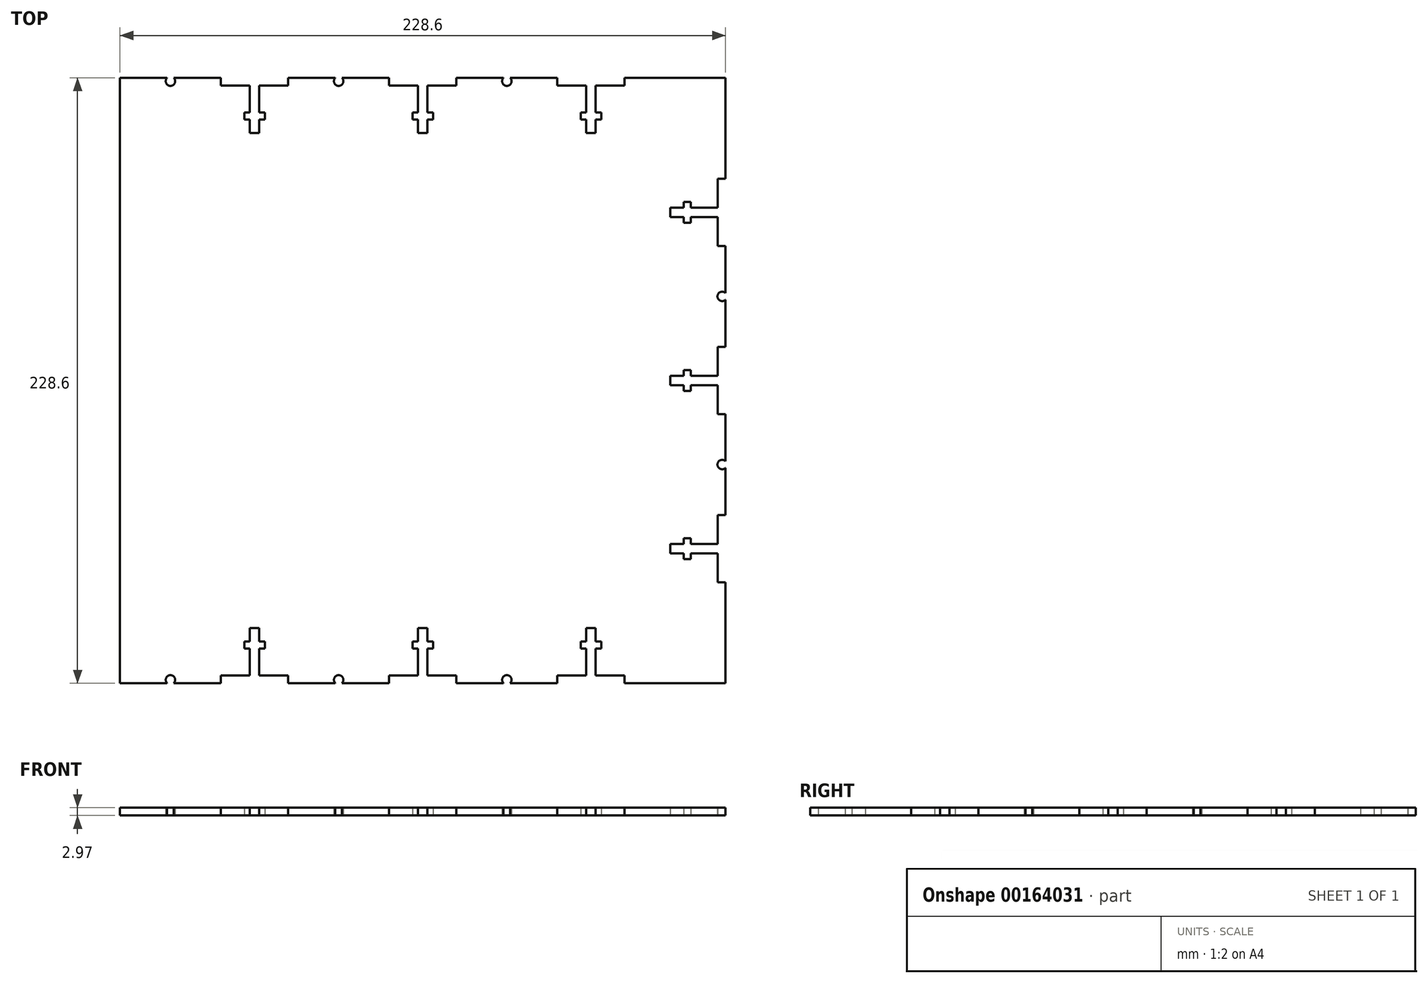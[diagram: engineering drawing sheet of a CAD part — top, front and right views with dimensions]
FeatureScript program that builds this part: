
annotation { "Feature Type Name" : "Feature", "Feature Type Description" : "" }
export const myFeature = defineFeature(function(context is Context, id is Id, definition is map)
    precondition{}
    {
        {
            var Q0;
            Q0=qCreatedBy(makeId("Top.planeOp"),FACE);
            var sketch = newSketch(context, id + "F0", { "sketchPlane" : qUnion([Q0])});
            skLineSegment(sketch, "E0.bottom", {"start": v(114.3, -114.3) * mm, "end": v(-114.3, -114.3) * mm});
            skLineSegment(sketch, "E0.top", {"start": v(114.3, 114.3) * mm, "end": v(-114.3, 114.3) * mm});
            skLineSegment(sketch, "E0.left", {"start": v(114.3, -114.3) * mm, "end": v(114.3, 114.3) * mm});
            skLineSegment(sketch, "E0.right", {"start": v(-114.3, -114.3) * mm, "end": v(-114.3, 114.3) * mm});
            skPoint(sketch, "E0.middle", {"position": v(0, 0) * mm});
            skLineSegment(sketch, "E1.bottom", {"start": v(-76.2, -114.3) * mm, "end": v(-50.8, -114.3) * mm});
            skLineSegment(sketch, "E1.top", {"start": v(-76.2, -111.33) * mm, "end": v(-65.27, -111.33) * mm});
            skLineSegment(sketch, "E1.left", {"start": v(-76.2, -114.3) * mm, "end": v(-76.2, -111.33) * mm});
            skLineSegment(sketch, "E1.right", {"start": v(-50.8, -114.3) * mm, "end": v(-50.8, -111.33) * mm});
            skArc(sketch, "E2", {"start": v(-94, -114.3) * mm, "mid": v(-95.25, -111.25) * mm, "end": v(-96.5, -114.3) * mm});
            skLineSegment(sketch, "E3.bottom", {"start": v(114.3, 76.2) * mm, "end": v(111.33, 76.2) * mm});
            skLineSegment(sketch, "E3.top", {"start": v(114.3, 50.8) * mm, "end": v(111.33, 50.8) * mm});
            skLineSegment(sketch, "E3.left", {"start": v(114.3, 76.2) * mm, "end": v(114.3, 50.8) * mm});
            skLineSegment(sketch, "E3.right", {"start": v(111.33, 76.2) * mm, "end": v(111.33, 50.8) * mm});
            skLineSegment(sketch, "E4.bottom", {"start": v(114.3, 12.7) * mm, "end": v(111.33, 12.7) * mm});
            skLineSegment(sketch, "E4.top", {"start": v(114.3, -12.7) * mm, "end": v(111.33, -12.7) * mm});
            skLineSegment(sketch, "E4.left", {"start": v(114.3, 12.7) * mm, "end": v(114.3, -12.7) * mm});
            skLineSegment(sketch, "E4.right", {"start": v(111.33, 12.7) * mm, "end": v(111.33, -12.7) * mm});
            skLineSegment(sketch, "E5.bottom", {"start": v(114.3, -50.8) * mm, "end": v(111.33, -50.8) * mm});
            skLineSegment(sketch, "E5.top", {"start": v(114.3, -76.2) * mm, "end": v(111.33, -76.2) * mm});
            skLineSegment(sketch, "E5.left", {"start": v(114.3, -50.8) * mm, "end": v(114.3, -76.2) * mm});
            skLineSegment(sketch, "E5.right", {"start": v(111.33, -50.8) * mm, "end": v(111.33, -61.73) * mm});
            skArc(sketch, "E6", {"start": v(114.3, 33) * mm, "mid": v(111.25, 31.75) * mm, "end": v(114.3, 30.5) * mm});
            skArc(sketch, "E7", {"start": v(114.3, -30.5) * mm, "mid": v(111.25, -31.75) * mm, "end": v(114.3, -33) * mm});
            skLineSegment(sketch, "E8.bottom", {"start": v(-65.27, -114.3) * mm, "end": v(-61.73, -114.3) * mm});
            skLineSegment(sketch, "E8.top", {"start": v(-65.27, -93.5) * mm, "end": v(-61.73, -93.5) * mm});
            skLineSegment(sketch, "E8.left", {"start": v(-65.27, -111.33) * mm, "end": v(-65.27, -101.17) * mm});
            skLineSegment(sketch, "E8.right", {"start": v(-61.73, -111.33) * mm, "end": v(-61.73, -101.17) * mm});
            skPoint(sketch, "E9", {"position": v(-63.5, -114.3) * mm});
            skLineSegment(sketch, "E10.trimOffspring", {"start": v(-61.73, -111.33) * mm, "end": v(-50.8, -111.33) * mm});
            skLineSegment(sketch, "E11", {"start": v(-63.5, -114.3) * mm, "end": v(-63.5, -89.69) * mm, "construction": true});
            skLineSegment(sketch, "E12.bottom", {"start": v(-59.61, -101.17) * mm, "end": v(-61.73, -101.17) * mm});
            skLineSegment(sketch, "E12.top", {"start": v(-59.61, -98.53) * mm, "end": v(-61.73, -98.53) * mm});
            skLineSegment(sketch, "E12.left", {"start": v(-59.61, -101.17) * mm, "end": v(-59.61, -98.53) * mm});
            skLineSegment(sketch, "E12.right", {"start": v(-67.39, -101.17) * mm, "end": v(-67.39, -98.53) * mm});
            skPoint(sketch, "E12.middle", {"position": v(-63.5, -99.85) * mm});
            skLineSegment(sketch, "E13.trimOffspring", {"start": v(-65.27, -98.53) * mm, "end": v(-65.27, -93.5) * mm});
            skLineSegment(sketch, "E14.trimOffspring", {"start": v(-61.73, -98.53) * mm, "end": v(-61.73, -93.5) * mm});
            skLineSegment(sketch, "E15.trimOffspring", {"start": v(-65.27, -98.53) * mm, "end": v(-67.39, -98.53) * mm});
            skLineSegment(sketch, "E16.trimOffspring", {"start": v(-65.27, -101.17) * mm, "end": v(-67.39, -101.17) * mm});
            skArc(sketch, "E17.1.0.0", {"start": v(-30.5, -114.3) * mm, "mid": v(-31.75, -111.25) * mm, "end": v(-33, -114.3) * mm});
            skLineSegment(sketch, "E17.1.0.1", {"start": v(-12.7, -114.3) * mm, "end": v(-12.7, -111.33) * mm});
            skLineSegment(sketch, "E17.1.0.2", {"start": v(-12.7, -114.3) * mm, "end": v(12.7, -114.3) * mm});
            skLineSegment(sketch, "E17.1.0.3", {"start": v(1.77, -111.33) * mm, "end": v(12.7, -111.33) * mm});
            skLineSegment(sketch, "E17.1.0.4", {"start": v(12.7, -114.3) * mm, "end": v(12.7, -111.33) * mm});
            skLineSegment(sketch, "E17.1.0.5", {"start": v(-12.7, -111.33) * mm, "end": v(-1.77, -111.33) * mm});
            skLineSegment(sketch, "E17.1.0.6", {"start": v(-1.77, -111.33) * mm, "end": v(-1.77, -101.17) * mm});
            skLineSegment(sketch, "E17.1.0.7", {"start": v(1.77, -111.33) * mm, "end": v(1.77, -101.17) * mm});
            skLineSegment(sketch, "E17.1.0.8", {"start": v(1.77, -98.53) * mm, "end": v(1.77, -93.5) * mm});
            skLineSegment(sketch, "E17.1.0.9", {"start": v(-1.77, -98.53) * mm, "end": v(-1.77, -93.5) * mm});
            skLineSegment(sketch, "E17.1.0.10", {"start": v(-1.77, -98.53) * mm, "end": v(-3.89, -98.53) * mm});
            skLineSegment(sketch, "E17.1.0.11", {"start": v(-3.89, -101.17) * mm, "end": v(-3.89, -98.53) * mm});
            skLineSegment(sketch, "E17.1.0.12", {"start": v(-1.77, -101.17) * mm, "end": v(-3.89, -101.17) * mm});
            skLineSegment(sketch, "E17.1.0.13", {"start": v(3.89, -101.17) * mm, "end": v(1.77, -101.17) * mm});
            skLineSegment(sketch, "E17.1.0.14", {"start": v(3.89, -98.53) * mm, "end": v(1.77, -98.53) * mm});
            skLineSegment(sketch, "E17.1.0.15", {"start": v(3.89, -101.17) * mm, "end": v(3.89, -98.53) * mm});
            skLineSegment(sketch, "E17.1.0.16", {"start": v(-1.77, -93.5) * mm, "end": v(1.77, -93.5) * mm});
            skArc(sketch, "E17.2.0.0", {"start": v(33, -114.3) * mm, "mid": v(31.75, -111.25) * mm, "end": v(30.5, -114.3) * mm});
            skLineSegment(sketch, "E17.2.0.1", {"start": v(50.8, -114.3) * mm, "end": v(50.8, -111.33) * mm});
            skLineSegment(sketch, "E17.2.0.2", {"start": v(50.8, -114.3) * mm, "end": v(76.2, -114.3) * mm});
            skLineSegment(sketch, "E17.2.0.3", {"start": v(65.27, -111.33) * mm, "end": v(76.2, -111.33) * mm});
            skLineSegment(sketch, "E17.2.0.4", {"start": v(76.2, -114.3) * mm, "end": v(76.2, -111.33) * mm});
            skLineSegment(sketch, "E17.2.0.5", {"start": v(50.8, -111.33) * mm, "end": v(61.73, -111.33) * mm});
            skLineSegment(sketch, "E17.2.0.6", {"start": v(61.73, -111.33) * mm, "end": v(61.73, -101.17) * mm});
            skLineSegment(sketch, "E17.2.0.7", {"start": v(65.27, -111.33) * mm, "end": v(65.27, -101.17) * mm});
            skLineSegment(sketch, "E17.2.0.8", {"start": v(65.27, -98.53) * mm, "end": v(65.27, -93.5) * mm});
            skLineSegment(sketch, "E17.2.0.9", {"start": v(61.73, -98.53) * mm, "end": v(61.73, -93.5) * mm});
            skLineSegment(sketch, "E17.2.0.10", {"start": v(61.73, -98.53) * mm, "end": v(59.61, -98.53) * mm});
            skLineSegment(sketch, "E17.2.0.11", {"start": v(59.61, -101.17) * mm, "end": v(59.61, -98.53) * mm});
            skLineSegment(sketch, "E17.2.0.12", {"start": v(61.73, -101.17) * mm, "end": v(59.61, -101.17) * mm});
            skLineSegment(sketch, "E17.2.0.13", {"start": v(67.39, -101.17) * mm, "end": v(65.27, -101.17) * mm});
            skLineSegment(sketch, "E17.2.0.14", {"start": v(67.39, -98.53) * mm, "end": v(65.27, -98.53) * mm});
            skLineSegment(sketch, "E17.2.0.15", {"start": v(67.39, -101.17) * mm, "end": v(67.39, -98.53) * mm});
            skLineSegment(sketch, "E17.2.0.16", {"start": v(61.73, -93.5) * mm, "end": v(65.27, -93.5) * mm});
            skLineSegment(sketch, "E17.direction1", {"start": v(-95.25, -113.03) * mm, "end": v(-31.75, -113.03) * mm, "construction": true});
            skArc(sketch, "E18.MirrorC", {"start": v(-94, 114.3) * mm, "mid": v(-95.25, 111.25) * mm, "end": v(-96.5, 114.3) * mm});
            skLineSegment(sketch, "E19.MirrorCS", {"start": v(-76.2, 114.3) * mm, "end": v(-76.2, 111.33) * mm});
            skLineSegment(sketch, "E20.MirrorCS", {"start": v(-76.2, 111.33) * mm, "end": v(-65.27, 111.33) * mm});
            skLineSegment(sketch, "E21.MirrorCS", {"start": v(-76.2, 114.3) * mm, "end": v(-50.8, 114.3) * mm});
            skLineSegment(sketch, "E22.MirrorCS", {"start": v(-50.8, 114.3) * mm, "end": v(-50.8, 111.33) * mm});
            skLineSegment(sketch, "E23.MirrorCS", {"start": v(-61.73, 111.33) * mm, "end": v(-50.8, 111.33) * mm});
            skLineSegment(sketch, "E24.MirrorCS", {"start": v(-61.73, 111.33) * mm, "end": v(-61.73, 101.17) * mm});
            skLineSegment(sketch, "E25.MirrorCS", {"start": v(-65.27, 111.33) * mm, "end": v(-65.27, 101.17) * mm});
            skLineSegment(sketch, "E26.MirrorCS", {"start": v(-65.27, 101.17) * mm, "end": v(-67.39, 101.17) * mm});
            skLineSegment(sketch, "E27.MirrorCS", {"start": v(-67.39, 101.17) * mm, "end": v(-67.39, 98.53) * mm});
            skLineSegment(sketch, "E28.MirrorCS", {"start": v(-65.27, 98.53) * mm, "end": v(-67.39, 98.53) * mm});
            skLineSegment(sketch, "E29.MirrorCS", {"start": v(-65.27, 98.53) * mm, "end": v(-65.27, 93.5) * mm});
            skLineSegment(sketch, "E30.MirrorCS", {"start": v(-65.27, 93.5) * mm, "end": v(-61.73, 93.5) * mm});
            skLineSegment(sketch, "E31.MirrorCS", {"start": v(-61.73, 98.53) * mm, "end": v(-61.73, 93.5) * mm});
            skLineSegment(sketch, "E32.MirrorCS", {"start": v(-59.61, 98.53) * mm, "end": v(-61.73, 98.53) * mm});
            skLineSegment(sketch, "E33.MirrorCS", {"start": v(-59.61, 101.17) * mm, "end": v(-59.61, 98.53) * mm});
            skLineSegment(sketch, "E34.MirrorCS", {"start": v(-59.61, 101.17) * mm, "end": v(-61.73, 101.17) * mm});
            skArc(sketch, "E35.MirrorC", {"start": v(-30.5, 114.3) * mm, "mid": v(-31.75, 111.25) * mm, "end": v(-33, 114.3) * mm});
            skLineSegment(sketch, "E36.MirrorCS", {"start": v(-12.7, 114.3) * mm, "end": v(-12.7, 111.33) * mm});
            skLineSegment(sketch, "E37.MirrorCS", {"start": v(-12.7, 114.3) * mm, "end": v(12.7, 114.3) * mm});
            skLineSegment(sketch, "E38.MirrorCS", {"start": v(-12.7, 111.33) * mm, "end": v(-1.77, 111.33) * mm});
            skLineSegment(sketch, "E39.MirrorCS", {"start": v(1.77, 111.33) * mm, "end": v(12.7, 111.33) * mm});
            skLineSegment(sketch, "E40.MirrorCS", {"start": v(12.7, 114.3) * mm, "end": v(12.7, 111.33) * mm});
            skLineSegment(sketch, "E41.MirrorCS", {"start": v(1.77, 111.33) * mm, "end": v(1.77, 101.17) * mm});
            skLineSegment(sketch, "E42.MirrorCS", {"start": v(-1.77, 111.33) * mm, "end": v(-1.77, 101.17) * mm});
            skLineSegment(sketch, "E43.MirrorCS", {"start": v(-1.77, 101.17) * mm, "end": v(-3.89, 101.17) * mm});
            skLineSegment(sketch, "E44.MirrorCS", {"start": v(-3.89, 101.17) * mm, "end": v(-3.89, 98.53) * mm});
            skLineSegment(sketch, "E45.MirrorCS", {"start": v(-1.77, 98.53) * mm, "end": v(-3.89, 98.53) * mm});
            skLineSegment(sketch, "E46.MirrorCS", {"start": v(-1.77, 98.53) * mm, "end": v(-1.77, 93.5) * mm});
            skLineSegment(sketch, "E47.MirrorCS", {"start": v(-1.77, 93.5) * mm, "end": v(1.77, 93.5) * mm});
            skLineSegment(sketch, "E48.MirrorCS", {"start": v(1.77, 98.53) * mm, "end": v(1.77, 93.5) * mm});
            skLineSegment(sketch, "E49.MirrorCS", {"start": v(3.89, 98.53) * mm, "end": v(1.77, 98.53) * mm});
            skLineSegment(sketch, "E50.MirrorCS", {"start": v(3.89, 101.17) * mm, "end": v(3.89, 98.53) * mm});
            skArc(sketch, "E51.MirrorC", {"start": v(33, 114.3) * mm, "mid": v(31.75, 111.25) * mm, "end": v(30.5, 114.3) * mm});
            skLineSegment(sketch, "E52.MirrorCS", {"start": v(50.8, 114.3) * mm, "end": v(76.2, 114.3) * mm});
            skLineSegment(sketch, "E53.MirrorCS", {"start": v(50.8, 114.3) * mm, "end": v(50.8, 111.33) * mm});
            skLineSegment(sketch, "E54.MirrorCS", {"start": v(50.8, 111.33) * mm, "end": v(61.73, 111.33) * mm});
            skLineSegment(sketch, "E55.MirrorCS", {"start": v(61.73, 111.33) * mm, "end": v(61.73, 101.17) * mm});
            skLineSegment(sketch, "E56.MirrorCS", {"start": v(61.73, 101.17) * mm, "end": v(59.61, 101.17) * mm});
            skLineSegment(sketch, "E57.MirrorCS", {"start": v(59.61, 101.17) * mm, "end": v(59.61, 98.53) * mm});
            skLineSegment(sketch, "E58.MirrorCS", {"start": v(61.73, 98.53) * mm, "end": v(59.61, 98.53) * mm});
            skLineSegment(sketch, "E59.MirrorCS", {"start": v(61.73, 98.53) * mm, "end": v(61.73, 93.5) * mm});
            skLineSegment(sketch, "E60.MirrorCS", {"start": v(61.73, 93.5) * mm, "end": v(65.27, 93.5) * mm});
            skLineSegment(sketch, "E61.MirrorCS", {"start": v(65.27, 98.53) * mm, "end": v(65.27, 93.5) * mm});
            skLineSegment(sketch, "E62.MirrorCS", {"start": v(67.39, 98.53) * mm, "end": v(65.27, 98.53) * mm});
            skLineSegment(sketch, "E63.MirrorCS", {"start": v(67.39, 101.17) * mm, "end": v(67.39, 98.53) * mm});
            skLineSegment(sketch, "E64.MirrorCS", {"start": v(67.39, 101.17) * mm, "end": v(65.27, 101.17) * mm});
            skLineSegment(sketch, "E65.MirrorCS", {"start": v(65.27, 111.33) * mm, "end": v(65.27, 101.17) * mm});
            skLineSegment(sketch, "E66.MirrorCS", {"start": v(65.27, 111.33) * mm, "end": v(76.2, 111.33) * mm});
            skLineSegment(sketch, "E67.MirrorCS", {"start": v(76.2, 114.3) * mm, "end": v(76.2, 111.33) * mm});
            skLineSegment(sketch, "E68.MirrorCS", {"start": v(3.89, 101.17) * mm, "end": v(1.77, 101.17) * mm});
            skPoint(sketch, "E69", {"position": v(114.3, -63.5) * mm});
            skLineSegment(sketch, "E70.bottom", {"start": v(111.33, -65.27) * mm, "end": v(93.5, -65.27) * mm});
            skLineSegment(sketch, "E70.top", {"start": v(111.33, -61.73) * mm, "end": v(93.5, -61.73) * mm});
            skLineSegment(sketch, "E70.left", {"start": v(114.3, -65.27) * mm, "end": v(114.3, -61.73) * mm});
            skLineSegment(sketch, "E70.right", {"start": v(93.5, -65.27) * mm, "end": v(93.5, -61.73) * mm});
            skPoint(sketch, "E70.middle", {"position": v(103.9, -63.5) * mm});
            skLineSegment(sketch, "E71.trimOffspring", {"start": v(111.33, -65.27) * mm, "end": v(111.33, -76.2) * mm});
            skLineSegment(sketch, "E72.0.1.0", {"start": v(111.33, 1.77) * mm, "end": v(93.5, 1.77) * mm});
            skLineSegment(sketch, "E72.0.1.1", {"start": v(111.33, -1.77) * mm, "end": v(93.5, -1.77) * mm});
            skLineSegment(sketch, "E72.0.1.2", {"start": v(93.5, -1.77) * mm, "end": v(93.5, 1.77) * mm});
            skLineSegment(sketch, "E72.direction1", {"start": v(93.5, -61.73) * mm, "end": v(118.9, -61.73) * mm, "construction": true});
            skLineSegment(sketch, "E72.direction2", {"start": v(93.5, -61.73) * mm, "end": v(93.5, 1.77) * mm, "construction": true});
            skLineSegment(sketch, "E73.0.0.2", {"start": v(111.33, 65.27) * mm, "end": v(93.5, 65.27) * mm});
            skLineSegment(sketch, "E73.3.0.2", {"start": v(111.33, 61.73) * mm, "end": v(93.5, 61.73) * mm});
            skLineSegment(sketch, "E73.6.0.2", {"start": v(93.5, 61.73) * mm, "end": v(93.5, 65.27) * mm});
            skLineSegment(sketch, "E74", {"start": v(103.9, -63.5) * mm, "end": v(82.71, -63.5) * mm, "construction": true});
            skLineSegment(sketch, "E75.bottom", {"start": v(101.17, -67.39) * mm, "end": v(98.53, -67.39) * mm});
            skLineSegment(sketch, "E75.top", {"start": v(101.17, -59.61) * mm, "end": v(98.53, -59.61) * mm});
            skLineSegment(sketch, "E75.left", {"start": v(101.17, -67.39) * mm, "end": v(101.17, -59.61) * mm});
            skLineSegment(sketch, "E75.right", {"start": v(98.53, -67.39) * mm, "end": v(98.53, -59.61) * mm});
            skPoint(sketch, "E75.middle", {"position": v(99.85, -63.5) * mm});
            skLineSegment(sketch, "E76.0.1.0", {"start": v(101.17, 3.89) * mm, "end": v(98.53, 3.89) * mm});
            skLineSegment(sketch, "E76.0.1.1", {"start": v(98.53, -3.89) * mm, "end": v(98.53, 3.89) * mm});
            skLineSegment(sketch, "E76.0.1.2", {"start": v(101.17, -3.89) * mm, "end": v(98.53, -3.89) * mm});
            skLineSegment(sketch, "E76.0.1.3", {"start": v(101.17, -3.89) * mm, "end": v(101.17, 3.89) * mm});
            skLineSegment(sketch, "E76.0.2.0", {"start": v(101.17, 67.39) * mm, "end": v(98.53, 67.39) * mm});
            skLineSegment(sketch, "E76.0.2.1", {"start": v(98.53, 59.61) * mm, "end": v(98.53, 67.39) * mm});
            skLineSegment(sketch, "E76.0.2.2", {"start": v(101.17, 59.61) * mm, "end": v(98.53, 59.61) * mm});
            skLineSegment(sketch, "E76.0.2.3", {"start": v(101.17, 59.61) * mm, "end": v(101.17, 67.39) * mm});
            skLineSegment(sketch, "E76.direction1", {"start": v(98.53, -59.61) * mm, "end": v(123.93, -59.61) * mm, "construction": true});
            skLineSegment(sketch, "E76.direction2", {"start": v(98.53, -59.61) * mm, "end": v(98.53, 3.89) * mm, "construction": true});
            skSolve(sketch);
        }
        {
            var Q0;
            {var subQ0=sQuery(id+"F0.wireOp",EDGE,"E17.2.0.0");var subQ1=sQuery(id+"F0.wireOp",EDGE,"E0.bottom");var subQ2=makeQuery(id+"F0.imprint","INTERSECT",VERTEX,{"disambiguationData":[OD(0.0)],"derivedFrom":[subQ1,subQ0]});Q0=makeQuery(id+"F0.imprint","IMPRINT",FACE,{"disambiguationData":[TD([[makeQuery(id+"F0.imprint","IMPRINT",EDGE,{"disambiguationData":[TD([[subQ2,-1.0]])],"derivedFrom":subQ1}),1.0]])]});}
            var Q1;
            {var subQ0=sQuery(id+"F0.wireOp",EDGE,"E17.1.0.0");var subQ1=sQuery(id+"F0.wireOp",EDGE,"E0.bottom");var subQ2=makeQuery(id+"F0.imprint","INTERSECT",VERTEX,{"disambiguationData":[OD(0.0)],"derivedFrom":[subQ1,subQ0]});Q1=makeQuery(id+"F0.imprint","IMPRINT",FACE,{"disambiguationData":[TD([[makeQuery(id+"F0.imprint","IMPRINT",EDGE,{"disambiguationData":[TD([[subQ2,-1.0]])],"derivedFrom":subQ1}),1.0]])]});}
            var Q2;
            {var subQ0=sQuery(id+"F0.wireOp",EDGE,"E2");var subQ1=sQuery(id+"F0.wireOp",EDGE,"E0.bottom");var subQ2=makeQuery(id+"F0.imprint","INTERSECT",VERTEX,{"disambiguationData":[OD(0.0)],"derivedFrom":[subQ1,subQ0]});Q2=makeQuery(id+"F0.imprint","IMPRINT",FACE,{"disambiguationData":[TD([[makeQuery(id+"F0.imprint","IMPRINT",EDGE,{"disambiguationData":[TD([[subQ2,-1.0]])],"derivedFrom":subQ1}),1.0]])]});}
            var Q3;
            {var subQ0=sQuery(id+"F0.wireOp",EDGE,"E51.MirrorC");var subQ1=sQuery(id+"F0.wireOp",EDGE,"E0.top");var subQ2=makeQuery(id+"F0.imprint","INTERSECT",VERTEX,{"disambiguationData":[OD(0.0)],"derivedFrom":[subQ1,subQ0]});Q3=makeQuery(id+"F0.imprint","IMPRINT",FACE,{"disambiguationData":[TD([[makeQuery(id+"F0.imprint","IMPRINT",EDGE,{"disambiguationData":[TD([[subQ2,-1.0]])],"derivedFrom":subQ1}),-1.0]])]});}
            var Q4;
            {var subQ0=sQuery(id+"F0.wireOp",EDGE,"E35.MirrorC");var subQ1=sQuery(id+"F0.wireOp",EDGE,"E0.top");var subQ2=makeQuery(id+"F0.imprint","INTERSECT",VERTEX,{"disambiguationData":[OD(0.0)],"derivedFrom":[subQ1,subQ0]});Q4=makeQuery(id+"F0.imprint","IMPRINT",FACE,{"disambiguationData":[TD([[makeQuery(id+"F0.imprint","IMPRINT",EDGE,{"disambiguationData":[TD([[subQ2,-1.0]])],"derivedFrom":subQ1}),-1.0]])]});}
            var Q5;
            {var subQ0=sQuery(id+"F0.wireOp",EDGE,"E18.MirrorC");var subQ1=sQuery(id+"F0.wireOp",EDGE,"E0.top");var subQ2=makeQuery(id+"F0.imprint","INTERSECT",VERTEX,{"disambiguationData":[OD(0.0)],"derivedFrom":[subQ1,subQ0]});Q5=makeQuery(id+"F0.imprint","IMPRINT",FACE,{"disambiguationData":[TD([[makeQuery(id+"F0.imprint","IMPRINT",EDGE,{"disambiguationData":[TD([[subQ2,-1.0]])],"derivedFrom":subQ1}),-1.0]])]});}
            var Q6;
            {var subQ0=sQuery(id+"F0.wireOp",EDGE,"E7");var subQ1=sQuery(id+"F0.wireOp",EDGE,"E0.left");var subQ2=makeQuery(id+"F0.imprint","INTERSECT",VERTEX,{"disambiguationData":[OD(0.0)],"derivedFrom":[subQ1,subQ0]});Q6=makeQuery(id+"F0.imprint","IMPRINT",FACE,{"disambiguationData":[TD([[makeQuery(id+"F0.imprint","IMPRINT",EDGE,{"disambiguationData":[TD([[subQ2,-1.0]])],"derivedFrom":subQ1}),-1.0]])]});}
            var Q7;
            {var subQ0=sQuery(id+"F0.wireOp",EDGE,"E6");var subQ1=sQuery(id+"F0.wireOp",EDGE,"E0.left");var subQ2=makeQuery(id+"F0.imprint","INTERSECT",VERTEX,{"disambiguationData":[OD(0.0)],"derivedFrom":[subQ1,subQ0]});Q7=makeQuery(id+"F0.imprint","IMPRINT",FACE,{"disambiguationData":[TD([[makeQuery(id+"F0.imprint","IMPRINT",EDGE,{"disambiguationData":[TD([[subQ2,-1.0]])],"derivedFrom":subQ1}),-1.0]])]});}
            var Q8;
            {var subQ1=sQuery(id+"F0.wireOp",EDGE,"E0.right");Q8=makeQuery(id+"F0.imprint","IMPRINT",FACE,{"disambiguationData":[TD([[makeQuery(id+"F0.imprint","IMPRINT",EDGE,{"derivedFrom":subQ1}),-1.0]])]});}
            extrude(context, id + "F1", {"entities" : qUnion([Q0, Q1, Q2, Q3, Q4, Q5, Q6, Q7, Q8]), "depth" : 2.97 * mm});
        }
    });
